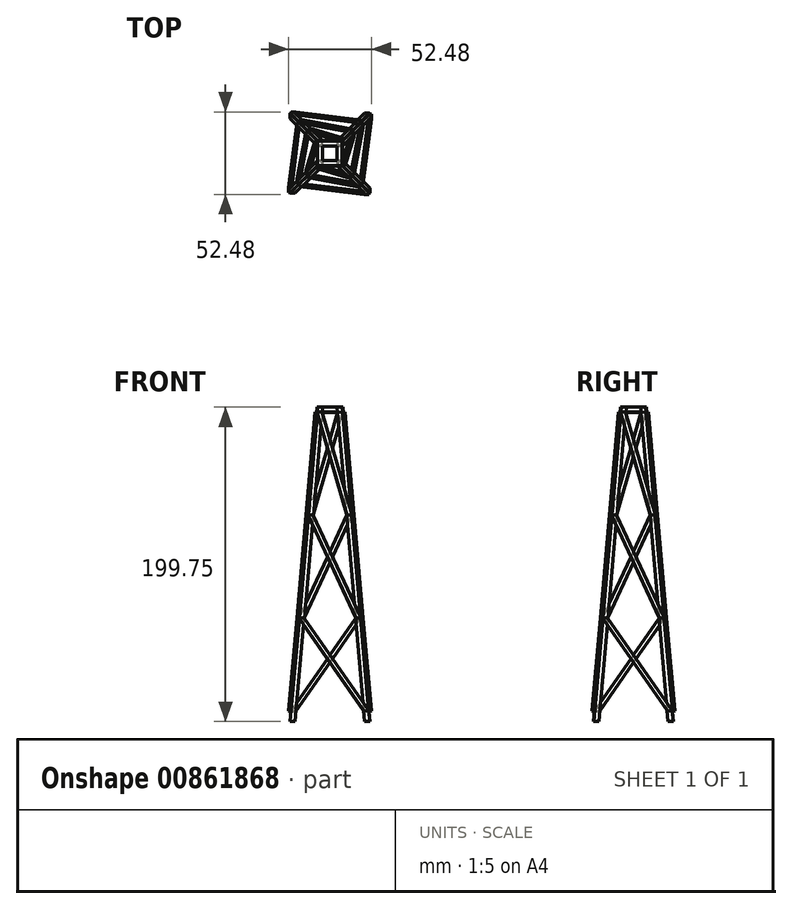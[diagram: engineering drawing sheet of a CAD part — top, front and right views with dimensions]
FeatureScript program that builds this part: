
annotation { "Feature Type Name" : "Feature", "Feature Type Description" : "" }
export const myFeature = defineFeature(function(context is Context, id is Id, definition is map)
    precondition{}
    {
        {
            var Q0;
            Q0=qCreatedBy(makeId("Top.planeOp"),FACE);
            var sketch = newSketch(context, id + "F0", { "sketchPlane" : qUnion([Q0])});
            skLineSegment(sketch, "E0", {"start": v(0, 0) * mm, "end": v(0, 116.82) * mm, "construction": true});
            skLineSegment(sketch, "E1", {"start": v(0, 0) * mm, "end": v(-140.82, 0) * mm, "construction": true});
            skSolve(sketch);
        }
        {
            var Q0;
            Q0=qCreatedBy(makeId("Right.planeOp"),FACE);
            var sketch = newSketch(context, id + "F1", { "sketchPlane" : qUnion([Q0])});
            skLineSegment(sketch, "E2", {"start": v(0, 0) * mm, "end": v(0, 196.85) * mm, "construction": true});
            skSolve(sketch);
        }
        {
            var Q0;
            Q0=qCreatedBy(makeId("Right.planeOp"),FACE);
            var sketch = newSketch(context, id + "F2", { "sketchPlane" : qUnion([Q0])});
            skPoint(sketch, "E3", {"position": v(-25.4, 0) * mm});
            skPoint(sketch, "E4.MirrorP", {"position": v(25.4, 0) * mm});
            skPoint(sketch, "E5", {"position": v(0, 290.32) * mm});
            skLineSegment(sketch, "E6", {"start": v(0, 290.32) * mm, "end": v(-25.4, 0) * mm, "construction": true});
            skLineSegment(sketch, "E7", {"start": v(0, 197.07) * mm, "end": v(-8.16, 197.07) * mm, "construction": true});
            skSolve(sketch);
        }
        {
            var Q0;
            Q0=sQuery(id+"F2.wireOp",EDGE,"E6");
            cPlane(context, id + "F3", {"entities" : qUnion([Q0]), "cplaneType" : CPlaneType.LINE_ANGLE, "offset" : 25.4 * mm, "angle" : 270 * degree, "width" : 152.4 * mm, "height" : 152.4 * mm});
        }
        {
            var Q0;
            Q0=qCreatedBy(id+"F3.planeOp",FACE);
            var sketch = newSketch(context, id + "F4", { "sketchPlane" : qUnion([Q0])});
            skLineSegment(sketch, "E8", {"start": v(-8.16, 197.06) * mm, "end": v(-25.4, 0) * mm});
            skLineSegment(sketch, "E9.0", {"start": v(-22.21, 0) * mm, "end": v(-4.97, 197.06) * mm});
            skLineSegment(sketch, "E10", {"start": v(-25.4, 0) * mm, "end": v(-22.24, 0) * mm});
            skPoint(sketch, "E11.orphan", {"position": v(0, 290.32) * mm});
            skLineSegment(sketch, "E12.MirrorCS", {"start": v(8.16, 197.06) * mm, "end": v(25.4, 0) * mm});
            skLineSegment(sketch, "E13.MirrorCS", {"start": v(22.21, 0) * mm, "end": v(4.97, 197.06) * mm});
            skLineSegment(sketch, "E14", {"start": v(-8.16, 197.06) * mm, "end": v(-4.97, 197.06) * mm});
            skLineSegment(sketch, "E15", {"start": v(-25.4, 0) * mm, "end": v(-22.21, 0) * mm});
            skLineSegment(sketch, "E16", {"start": v(4.97, 197.06) * mm, "end": v(8.16, 197.06) * mm});
            skLineSegment(sketch, "E17", {"start": v(22.21, 0) * mm, "end": v(25.4, 0) * mm});
            skLineSegment(sketch, "E18", {"start": v(-8.16, 197.06) * mm, "end": v(8.16, 197.06) * mm});
            skLineSegment(sketch, "E19", {"start": v(8.16, 200.23) * mm, "end": v(8.16, 197.06) * mm});
            skLineSegment(sketch, "E20", {"start": v(8.16, 200.23) * mm, "end": v(-8.16, 200.23) * mm});
            skLineSegment(sketch, "E21", {"start": v(-8.16, 200.23) * mm, "end": v(-8.16, 197.06) * mm});
            skLineSegment(sketch, "E22", {"start": v(52.04, 197.06) * mm, "end": v(52.04, 0) * mm, "construction": true});
            skLineSegment(sketch, "E23", {"start": v(31.34, 0) * mm, "end": v(31.34, 6.35) * mm, "construction": true});
            skLineSegment(sketch, "E24", {"start": v(31.34, 6.35) * mm, "end": v(-63.34, 6.35) * mm, "construction": true});
            skLineSegment(sketch, "E25", {"start": v(24.84, 6.35) * mm, "end": v(21.66, 6.35) * mm});
            skLineSegment(sketch, "E26", {"start": v(40.88, 197.06) * mm, "end": v(40.88, 131.37) * mm, "construction": true});
            skLineSegment(sketch, "E27", {"start": v(40.88, 131.37) * mm, "end": v(40.88, 65.69) * mm, "construction": true});
            skLineSegment(sketch, "E28", {"start": v(40.88, 65.69) * mm, "end": v(40.88, 0) * mm, "construction": true});
            skLineSegment(sketch, "E29", {"start": v(40.88, 65.69) * mm, "end": v(-70.33, 65.69) * mm, "construction": true});
            skLineSegment(sketch, "E30", {"start": v(40.88, 131.37) * mm, "end": v(-29.1, 131.37) * mm, "construction": true});
            skLineSegment(sketch, "E31", {"start": v(-4.97, 197.06) * mm, "end": v(13.9, 131.37) * mm});
            skLineSegment(sketch, "E32", {"start": v(13.9, 131.37) * mm, "end": v(10.72, 131.37) * mm});
            skLineSegment(sketch, "E33", {"start": v(10.72, 131.37) * mm, "end": v(-8.16, 197.06) * mm});
            skLineSegment(sketch, "E34", {"start": v(-10.72, 131.37) * mm, "end": v(19.65, 65.69) * mm});
            skLineSegment(sketch, "E35", {"start": v(19.65, 65.69) * mm, "end": v(16.47, 65.69) * mm});
            skLineSegment(sketch, "E36", {"start": v(16.47, 65.69) * mm, "end": v(-13.9, 131.37) * mm});
            skLineSegment(sketch, "E37", {"start": v(-13.9, 131.37) * mm, "end": v(-10.72, 131.37) * mm});
            skLineSegment(sketch, "E38", {"start": v(-16.47, 65.69) * mm, "end": v(24.84, 6.35) * mm});
            skLineSegment(sketch, "E39", {"start": v(21.66, 6.35) * mm, "end": v(-19.65, 65.69) * mm});
            skLineSegment(sketch, "E40", {"start": v(-19.65, 65.69) * mm, "end": v(-16.47, 65.69) * mm});
            skSolve(sketch);
        }
        {
            var Q0;
            {var subQ0=sQuery(id+"F4.wireOp",EDGE,"E19");Q0=makeQuery(id+"F4.imprint","IMPRINT",FACE,{"disambiguationData":[TD([[makeQuery(id+"F4.imprint","IMPRINT",EDGE,{"derivedFrom":subQ0}),-1.0]])]});}
            extrude(context, id + "F5", {"entities" : qUnion([Q0]), "oppositeDirection" : true, "depth" : 3.17 * mm, "offsetDistance" : 25.4 * mm});
        }
        {
            var Q0;
            {var subQ3=sQuery(id+"F4.wireOp",EDGE,"E25");Q0=makeQuery(id+"F4.imprint","IMPRINT",FACE,{"disambiguationData":[TD([[makeQuery(id+"F4.imprint","IMPRINT",EDGE,{"derivedFrom":subQ3}),-1.0]])]});}
            var Q1;
            {var subQ0=sQuery(id+"F4.wireOp",EDGE,"E18");var subQ5=sQuery(id+"F4.wireOp",EDGE,"E13.MirrorCS");var subQ6=makeQuery(id+"F4.imprint","INTERSECT",VERTEX,{"derivedFrom":[subQ5,subQ0]});Q1=makeQuery(id+"F4.imprint","IMPRINT",FACE,{"disambiguationData":[TD([[makeQuery(id+"F4.imprint","IMPRINT",EDGE,{"disambiguationData":[TD([[subQ6,1.0]])],"derivedFrom":subQ5}),-1.0]])]});}
            var Q2;
            {var subQ0=sQuery(id+"F4.wireOp",EDGE,"E32");Q2=makeQuery(id+"F4.imprint","IMPRINT",FACE,{"disambiguationData":[TD([[makeQuery(id+"F4.imprint","IMPRINT",EDGE,{"derivedFrom":subQ0}),-1.0]])]});}
            var Q3;
            {var subQ0=sQuery(id+"F4.wireOp",EDGE,"E32");Q3=makeQuery(id+"F4.imprint","IMPRINT",FACE,{"disambiguationData":[TD([[makeQuery(id+"F4.imprint","IMPRINT",EDGE,{"derivedFrom":subQ0}),1.0]])]});}
            var Q4;
            {var subQ0=sQuery(id+"F4.wireOp",EDGE,"E35");Q4=makeQuery(id+"F4.imprint","IMPRINT",FACE,{"disambiguationData":[TD([[makeQuery(id+"F4.imprint","IMPRINT",EDGE,{"derivedFrom":subQ0}),-1.0]])]});}
            var Q5;
            {var subQ3=sQuery(id+"F4.wireOp",EDGE,"E35");Q5=makeQuery(id+"F4.imprint","IMPRINT",FACE,{"disambiguationData":[TD([[makeQuery(id+"F4.imprint","IMPRINT",EDGE,{"derivedFrom":subQ3}),1.0]])]});}
            var Q6;
            {var subQ0=sQuery(id+"F4.wireOp",EDGE,"E17");Q6=makeQuery(id+"F4.imprint","IMPRINT",FACE,{"disambiguationData":[TD([[makeQuery(id+"F4.imprint","IMPRINT",EDGE,{"derivedFrom":subQ0}),1.0]])]});}
            extrude(context, id + "F6", {"entities" : qUnion([Q0, Q1, Q2, Q3, Q4, Q5, Q6]), "oppositeDirection" : true, "depth" : 3.17 * mm, "offsetDistance" : 25.4 * mm});
        }
        {
            var Q0;
            {var subQ1=sQuery(id+"F4.wireOp",EDGE,"E9.0");var subQ3=sQuery(id+"F4.wireOp",EDGE,"E33");var subQ4=makeQuery(id+"F4.imprint","INTERSECT",VERTEX,{"derivedFrom":[subQ1,subQ3]});Q0=makeQuery(id+"F4.imprint","IMPRINT",FACE,{"disambiguationData":[TD([[makeQuery(id+"F4.imprint","IMPRINT",EDGE,{"disambiguationData":[TD([[subQ4,-1.0]])],"derivedFrom":subQ1}),1.0]])]});}
            var Q1;
            {var subQ3=sQuery(id+"F4.wireOp",EDGE,"E37");Q1=makeQuery(id+"F4.imprint","IMPRINT",FACE,{"disambiguationData":[TD([[makeQuery(id+"F4.imprint","IMPRINT",EDGE,{"derivedFrom":subQ3}),1.0]])]});}
            var Q2;
            {var subQ3=sQuery(id+"F4.wireOp",EDGE,"E40");Q2=makeQuery(id+"F4.imprint","IMPRINT",FACE,{"disambiguationData":[TD([[makeQuery(id+"F4.imprint","IMPRINT",EDGE,{"derivedFrom":subQ3}),1.0]])]});}
            var Q3;
            {var subQ0=sQuery(id+"F4.wireOp",EDGE,"E37");Q3=makeQuery(id+"F4.imprint","IMPRINT",FACE,{"disambiguationData":[TD([[makeQuery(id+"F4.imprint","IMPRINT",EDGE,{"derivedFrom":subQ0}),-1.0]])]});}
            var Q4;
            {var subQ0=sQuery(id+"F4.wireOp",EDGE,"E40");Q4=makeQuery(id+"F4.imprint","IMPRINT",FACE,{"disambiguationData":[TD([[makeQuery(id+"F4.imprint","IMPRINT",EDGE,{"derivedFrom":subQ0}),-1.0]])]});}
            var Q5;
            {var subQ0=sQuery(id+"F4.wireOp",EDGE,"E15");var subQ5=sQuery(id+"F4.wireOp",EDGE,"E9.0");var subQ6=makeQuery(id+"F4.imprint","INTERSECT",VERTEX,{"derivedFrom":[subQ5,subQ0]});Q5=makeQuery(id+"F4.imprint","IMPRINT",FACE,{"disambiguationData":[TD([[makeQuery(id+"F4.imprint","IMPRINT",EDGE,{"disambiguationData":[TD([[subQ6,-1.0]])],"derivedFrom":subQ5}),1.0]])]});}
            extrude(context, id + "F7", {"entities" : qUnion([Q0, Q1, Q2, Q3, Q4, Q5]), "operationType" : NewBodyOperationType.ADD, "oppositeDirection" : true, "depth" : 3.17 * mm, "offsetDistance" : 25.4 * mm});
        }
        {
            var Q0;
            {var subQ1=sQuery(id+"F4.wireOp",EDGE,"E9.0");var subQ3=sQuery(id+"F4.wireOp",EDGE,"E39");var subQ4=makeQuery(id+"F4.imprint","INTERSECT",VERTEX,{"derivedFrom":[subQ1,subQ3]});Q0=makeQuery(id+"F4.imprint","IMPRINT",FACE,{"disambiguationData":[TD([[makeQuery(id+"F4.imprint","IMPRINT",EDGE,{"disambiguationData":[TD([[subQ4,-1.0]])],"derivedFrom":subQ1}),-1.0]])]});}
            var Q1;
            {var subQ0=sQuery(id+"F4.wireOp",EDGE,"E40");Q1=makeQuery(id+"F4.imprint","IMPRINT",FACE,{"disambiguationData":[TD([[makeQuery(id+"F4.imprint","IMPRINT",EDGE,{"derivedFrom":subQ0}),-1.0]])]});}
            var Q2;
            {var subQ0=sQuery(id+"F4.wireOp",EDGE,"E37");Q2=makeQuery(id+"F4.imprint","IMPRINT",FACE,{"disambiguationData":[TD([[makeQuery(id+"F4.imprint","IMPRINT",EDGE,{"derivedFrom":subQ0}),-1.0]])]});}
            var Q3;
            {var subQ1=sQuery(id+"F4.wireOp",EDGE,"E9.0");var subQ3=sQuery(id+"F4.wireOp",EDGE,"E33");var subQ4=makeQuery(id+"F4.imprint","INTERSECT",VERTEX,{"derivedFrom":[subQ1,subQ3]});Q3=makeQuery(id+"F4.imprint","IMPRINT",FACE,{"disambiguationData":[TD([[makeQuery(id+"F4.imprint","IMPRINT",EDGE,{"disambiguationData":[TD([[subQ4,-1.0]])],"derivedFrom":subQ1}),1.0]])]});}
            var Q4;
            {var subQ0=sQuery(id+"F4.wireOp",EDGE,"E25");Q4=makeQuery(id+"F4.imprint","IMPRINT",FACE,{"disambiguationData":[TD([[makeQuery(id+"F4.imprint","IMPRINT",EDGE,{"derivedFrom":subQ0}),-1.0]])]});}
            var Q5;
            {var subQ0=sQuery(id+"F4.wireOp",EDGE,"E35");Q5=makeQuery(id+"F4.imprint","IMPRINT",FACE,{"disambiguationData":[TD([[makeQuery(id+"F4.imprint","IMPRINT",EDGE,{"derivedFrom":subQ0}),-1.0]])]});}
            var Q6;
            {var subQ0=sQuery(id+"F4.wireOp",EDGE,"E32");Q6=makeQuery(id+"F4.imprint","IMPRINT",FACE,{"disambiguationData":[TD([[makeQuery(id+"F4.imprint","IMPRINT",EDGE,{"derivedFrom":subQ0}),-1.0]])]});}
            var Q7;
            {var subQ1=sQuery(id+"F4.wireOp",EDGE,"E9.0");var subQ3=sQuery(id+"F4.wireOp",EDGE,"E36");var subQ4=makeQuery(id+"F4.imprint","INTERSECT",VERTEX,{"derivedFrom":[subQ1,subQ3]});Q7=makeQuery(id+"F4.imprint","IMPRINT",FACE,{"disambiguationData":[TD([[makeQuery(id+"F4.imprint","IMPRINT",EDGE,{"disambiguationData":[TD([[subQ4,-1.0]])],"derivedFrom":subQ1}),-1.0]])]});}
            var Q8;
            {var subQ1=sQuery(id+"F4.wireOp",EDGE,"E9.0");var subQ3=sQuery(id+"F4.wireOp",EDGE,"E33");var subQ4=makeQuery(id+"F4.imprint","INTERSECT",VERTEX,{"derivedFrom":[subQ1,subQ3]});Q8=makeQuery(id+"F4.imprint","IMPRINT",FACE,{"disambiguationData":[TD([[makeQuery(id+"F4.imprint","IMPRINT",EDGE,{"disambiguationData":[TD([[subQ4,-1.0]])],"derivedFrom":subQ1}),-1.0]])]});}
            extrude(context, id + "F8", {"entities" : qUnion([Q0, Q1, Q2, Q3, Q4, Q5, Q6, Q7, Q8]), "depth" : 1.59 * mm, "offsetDistance" : 25.4 * mm});
        }
        {
            var Q0;
            Q0=makeQuery(id+"F5.opExtrude","SWEPT_BODY",BODY,{"disambiguationData":[OSD([sQuery(id+"F4.wireOp",EDGE,"E18"),sQuery(id+"F4.wireOp",EDGE,"E19"),sQuery(id+"F4.wireOp",EDGE,"E20"),sQuery(id+"F4.wireOp",EDGE,"E21")])]});
            var Q1;
            Q1=makeQuery(id+"F6.opExtrude","SWEPT_BODY",BODY,{"disambiguationData":[OSD([sQuery(id+"F4.wireOp",EDGE,"E12.MirrorCS"),sQuery(id+"F4.wireOp",EDGE,"E13.MirrorCS"),sQuery(id+"F4.wireOp",EDGE,"E17"),sQuery(id+"F4.wireOp",EDGE,"E18")])]});
            var Q2;
            Q2=makeQuery(id+"F8.opExtrude","SWEPT_BODY",BODY,{"disambiguationData":[OSD([sQuery(id+"F4.wireOp",EDGE,"E18"),sQuery(id+"F4.wireOp",EDGE,"E31"),sQuery(id+"F4.wireOp",EDGE,"E32"),sQuery(id+"F4.wireOp",EDGE,"E33")])]});
            var Q3;
            Q3=makeQuery(id+"F8.opExtrude","SWEPT_BODY",BODY,{"disambiguationData":[OSD([sQuery(id+"F4.wireOp",EDGE,"E34"),sQuery(id+"F4.wireOp",EDGE,"E35"),sQuery(id+"F4.wireOp",EDGE,"E36"),sQuery(id+"F4.wireOp",EDGE,"E37")])]});
            var Q4;
            Q4=makeQuery(id+"F8.opExtrude","SWEPT_BODY",BODY,{"disambiguationData":[OSD([sQuery(id+"F4.wireOp",EDGE,"E25"),sQuery(id+"F4.wireOp",EDGE,"E38"),sQuery(id+"F4.wireOp",EDGE,"E39"),sQuery(id+"F4.wireOp",EDGE,"E40")])]});
            var Q5;
            Q5=sQuery(id+"F1.wireOp",EDGE,"E2");
            circularPattern(context, id + "F9", {"entities" : qUnion([Q0, Q1, Q2, Q3, Q4]), "axis" : qUnion([Q5]), "angle" : 360 * degree, "instanceCount" : 4, "equalSpace" : true});
        }
    });
